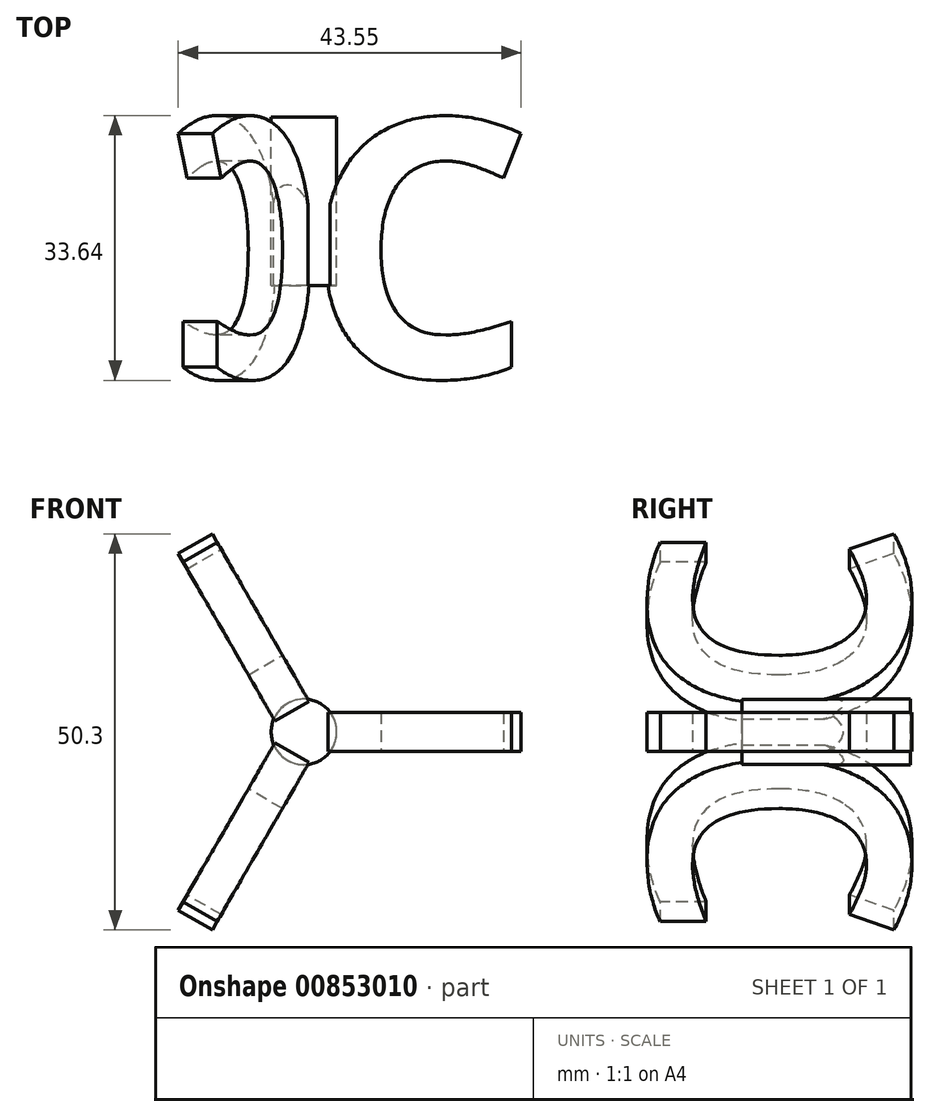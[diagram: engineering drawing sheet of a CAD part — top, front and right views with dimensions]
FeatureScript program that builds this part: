
annotation { "Feature Type Name" : "Feature", "Feature Type Description" : "" }
export const myFeature = defineFeature(function(context is Context, id is Id, definition is map)
    precondition{}
    {
        {
            var Q0;
            Q0=qCreatedBy(makeId("Top.planeOp"),FACE);
            var sketch = newSketch(context, id + "F0", { "sketchPlane" : qUnion([Q0])});
            skText(sketch, "E0", { "text": "C", "fontName": "OpenSans-Bold.ttf"});
            skLineSegment(sketch, "E1", {"start": v(0, 0) * mm, "end": v(0, -33) * mm});
            const initialGuessF0  = {"E0": [0, -0.033, 1, 0, 0.033]};
            skSetInitialGuess(sketch, initialGuessF0);
            skSolve(sketch);
        }
        {
            var Q0;
            Q0=makeQuery(id+"F0.imprint","IMPRINT",FACE,{"disambiguationData":[TD([[makeQuery(id+"F0.imprint","IMPRINT",EDGE,{"derivedFrom":sQuery(id+"F0.wireOp",EDGE,"E0.sketch_text.stroke-0")}),-1.0]])]});
            extrude(context, id + "F1", {"entities" : qUnion([Q0]), "endBound" : BoundingType.SYMMETRIC, "depth" : 5 * mm, "offsetDistance" : 25 * mm});
        }
        {
            var Q0;
            Q0=qCreatedBy(makeId("Front.planeOp"),FACE);
            var sketch = newSketch(context, id + "F2", { "sketchPlane" : qUnion([Q0])});
            skCircle(sketch, "E2", {"center": v(0, 0) * mm, "radius": 4.17 * mm});
            skSolve(sketch);
        }
        {
            var Q0;
            Q0 = qSketchRegion(id + "F2", true);
            extrude(context, id + "F3", {"entities" : qUnion([Q0]), "operationType" : NewBodyOperationType.ADD, "depth" : 21.4 * mm, "offsetDistance" : 25 * mm});
        }
        {
            var Q0;
            Q0=makeQuery(id+"F1.opExtrude","SWEPT_BODY",BODY,{"disambiguationData":[OSD([sQuery(id+"F0.wireOp",EDGE,"E0.sketch_text.stroke-0"),sQuery(id+"F0.wireOp",EDGE,"E0.sketch_text.stroke-1"),sQuery(id+"F0.wireOp",EDGE,"E0.sketch_text.stroke-2"),sQuery(id+"F0.wireOp",EDGE,"E0.sketch_text.stroke-3"),sQuery(id+"F0.wireOp",EDGE,"E0.sketch_text.stroke-4"),sQuery(id+"F0.wireOp",EDGE,"E0.sketch_text.stroke-5"),sQuery(id+"F0.wireOp",EDGE,"E0.sketch_text.stroke-6"),sQuery(id+"F0.wireOp",EDGE,"E0.sketch_text.stroke-7"),sQuery(id+"F0.wireOp",EDGE,"E0.sketch_text.stroke-8"),sQuery(id+"F0.wireOp",EDGE,"E0.sketch_text.stroke-9"),sQuery(id+"F0.wireOp",EDGE,"E0.sketch_text.stroke-10"),sQuery(id+"F0.wireOp",EDGE,"E0.sketch_text.stroke-11"),sQuery(id+"F0.wireOp",EDGE,"E0.sketch_text.stroke-12"),sQuery(id+"F0.wireOp",EDGE,"E0.sketch_text.stroke-13"),sQuery(id+"F0.wireOp",EDGE,"E0.sketch_text.stroke-14")])]});
            var Q1;
            Q1=makeQuery(id+"F3.opExtrude","SWEPT_FACE",FACE,{"disambiguationData":[OSD([sQuery(id+"F2.wireOp",EDGE,"E2")])]});
            circularPattern(context, id + "F4", {"entities" : qUnion([Q0]), "axis" : qUnion([Q1]), "angle" : 360 * degree, "instanceCount" : 3, "equalSpace" : true});
        }
    });
